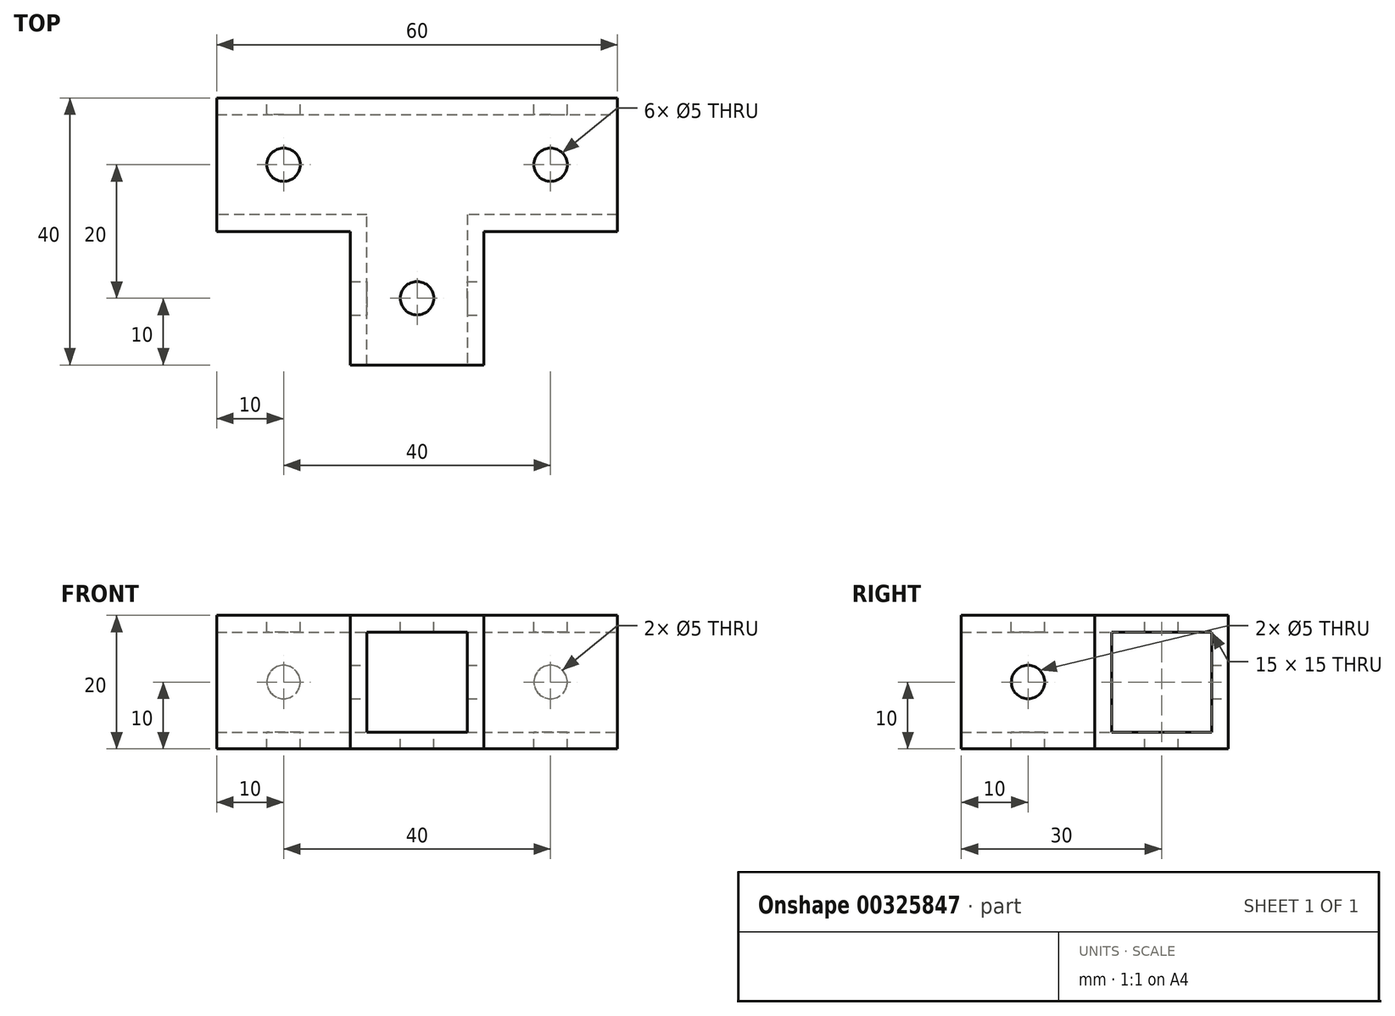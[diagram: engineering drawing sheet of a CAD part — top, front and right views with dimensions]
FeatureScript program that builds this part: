
annotation { "Feature Type Name" : "Feature", "Feature Type Description" : "" }
export const myFeature = defineFeature(function(context is Context, id is Id, definition is map)
    precondition{}
    {
        {
            var Q0;
            Q0=qCreatedBy(makeId("Top.planeOp"),FACE);
            var sketch = newSketch(context, id + "F0", { "sketchPlane" : qUnion([Q0])});
            skLineSegment(sketch, "E0", {"start": v(-30, 0) * mm, "end": v(30, 0) * mm});
            skLineSegment(sketch, "E1", {"start": v(30, 0) * mm, "end": v(30, -20) * mm});
            skLineSegment(sketch, "E2", {"start": v(30, -20) * mm, "end": v(10, -20) * mm});
            skLineSegment(sketch, "E3", {"start": v(10, -20) * mm, "end": v(10, -40) * mm});
            skLineSegment(sketch, "E4", {"start": v(10, -40) * mm, "end": v(-10, -40) * mm});
            skLineSegment(sketch, "E5", {"start": v(-10, -40) * mm, "end": v(-10, -20) * mm});
            skLineSegment(sketch, "E6", {"start": v(-10, -20) * mm, "end": v(-30, -20) * mm});
            skLineSegment(sketch, "E7", {"start": v(-30, -20) * mm, "end": v(-30, 0) * mm});
            skSolve(sketch);
        }
        {
            var Q0;
            Q0 = qSketchRegion(id + "F0", true);
            extrude(context, id + "F1", {"entities" : qUnion([Q0]), "oppositeDirection" : true, "depth" : 20 * mm});
        }
        {
            var Q0;
            Q0=makeQuery(id+"F1.opExtrude","SWEPT_FACE",FACE,{"disambiguationData":[OSD([sQuery(id+"F0.wireOp",EDGE,"E1")])]});
            var Q1;
            Q1=makeQuery(id+"F1.opExtrude","SWEPT_FACE",FACE,{"disambiguationData":[OSD([sQuery(id+"F0.wireOp",EDGE,"E4")])]});
            var Q2;
            Q2=makeQuery(id+"F1.opExtrude","SWEPT_FACE",FACE,{"disambiguationData":[OSD([sQuery(id+"F0.wireOp",EDGE,"E7")])]});
            shell(context, id + "F2", {"entities" : qUnion([Q0, Q1, Q2]), "thickness" : 2.5 * mm});
        }
        {
            var Q0;
            Q0=makeQuery(id+"F1.opExtrude","CAP_FACE",FACE,{"disambiguationData":[OSD([sQuery(id+"F0.wireOp",EDGE,"E0"),sQuery(id+"F0.wireOp",EDGE,"E1"),sQuery(id+"F0.wireOp",EDGE,"E2"),sQuery(id+"F0.wireOp",EDGE,"E3"),sQuery(id+"F0.wireOp",EDGE,"E4"),sQuery(id+"F0.wireOp",EDGE,"E5"),sQuery(id+"F0.wireOp",EDGE,"E6"),sQuery(id+"F0.wireOp",EDGE,"E7")])],"isStart":true});
            var sketch = newSketch(context, id + "F3", { "sketchPlane" : qUnion([Q0])});
            skLineSegment(sketch, "E8", {"start": v(-10, -20) * mm, "end": v(-10, 0) * mm, "construction": true});
            skLineSegment(sketch, "E9", {"start": v(-10, -20) * mm, "end": v(10, -20) * mm, "construction": true});
            skLineSegment(sketch, "E10", {"start": v(10, -20) * mm, "end": v(10, 0) * mm, "construction": true});
            skLineSegment(sketch, "E11", {"start": v(10, 0) * mm, "end": v(30, 0) * mm, "construction": true});
            skLineSegment(sketch, "E12", {"start": v(30, 0) * mm, "end": v(30, -20) * mm, "construction": true});
            skLineSegment(sketch, "E13", {"start": v(30, -20) * mm, "end": v(10, -20) * mm, "construction": true});
            skLineSegment(sketch, "E14", {"start": v(10, -40) * mm, "end": v(10, -20) * mm, "construction": true});
            skLineSegment(sketch, "E15", {"start": v(10, -40) * mm, "end": v(-10, -40) * mm, "construction": true});
            skLineSegment(sketch, "E16", {"start": v(-10, -40) * mm, "end": v(-10, -20) * mm, "construction": true});
            skLineSegment(sketch, "E17", {"start": v(-30, -20) * mm, "end": v(-10, -20) * mm, "construction": true});
            skLineSegment(sketch, "E18", {"start": v(-30, -20) * mm, "end": v(-30, 0) * mm, "construction": true});
            skLineSegment(sketch, "E19", {"start": v(-30, 0) * mm, "end": v(-10, 0) * mm, "construction": true});
            skLineSegment(sketch, "E20", {"start": v(-30, -20) * mm, "end": v(-10, 0) * mm, "construction": true});
            skLineSegment(sketch, "E21", {"start": v(-30, 0) * mm, "end": v(-10, -20) * mm, "construction": true});
            skLineSegment(sketch, "E22", {"start": v(-10, -20) * mm, "end": v(10, -40) * mm, "construction": true});
            skLineSegment(sketch, "E23", {"start": v(10, -20) * mm, "end": v(-10, -40) * mm, "construction": true});
            skLineSegment(sketch, "E24", {"start": v(10, -20) * mm, "end": v(30, 0) * mm, "construction": true});
            skLineSegment(sketch, "E25", {"start": v(10, 0) * mm, "end": v(30, -20) * mm, "construction": true});
            skCircle(sketch, "E26", {"center": v(-20, -10) * mm, "radius": 2.5 * mm});
            skCircle(sketch, "E27", {"center": v(20, -10) * mm, "radius": 2.5 * mm});
            skCircle(sketch, "E28", {"center": v(0, -30) * mm, "radius": 2.5 * mm});
            skSolve(sketch);
        }
        {
            var Q0;
            Q0 = qSketchRegion(id + "F3", true);
            extrude(context, id + "F4", {"entities" : qUnion([Q0]), "operationType" : NewBodyOperationType.REMOVE, "endBound" : BoundingType.THROUGH_ALL, "oppositeDirection" : true, "depth" : 25 * mm});
        }
        {
            var Q0;
            Q0=makeQuery(id+"F1.opExtrude","SWEPT_FACE",FACE,{"disambiguationData":[OSD([sQuery(id+"F0.wireOp",EDGE,"E0")])]});
            var sketch = newSketch(context, id + "F5", { "sketchPlane" : qUnion([Q0])});
            skLineSegment(sketch, "E29", {"start": v(-30, 0) * mm, "end": v(-10, 0) * mm, "construction": true});
            skLineSegment(sketch, "E30", {"start": v(-10, 0) * mm, "end": v(-10, -20) * mm, "construction": true});
            skLineSegment(sketch, "E31", {"start": v(-10, -20) * mm, "end": v(-30, -20) * mm, "construction": true});
            skLineSegment(sketch, "E32", {"start": v(-30, -20) * mm, "end": v(-30, 0) * mm, "construction": true});
            skLineSegment(sketch, "E33", {"start": v(30, 0) * mm, "end": v(30, -20) * mm, "construction": true});
            skLineSegment(sketch, "E34", {"start": v(30, -20) * mm, "end": v(10, -20) * mm, "construction": true});
            skLineSegment(sketch, "E35", {"start": v(10, -20) * mm, "end": v(10, 0) * mm, "construction": true});
            skLineSegment(sketch, "E36", {"start": v(10, 0) * mm, "end": v(30, 0) * mm, "construction": true});
            skLineSegment(sketch, "E37", {"start": v(10, 0) * mm, "end": v(30, -20) * mm, "construction": true});
            skLineSegment(sketch, "E38", {"start": v(30, 0) * mm, "end": v(10, -20) * mm, "construction": true});
            skLineSegment(sketch, "E39", {"start": v(-30, 0) * mm, "end": v(-10, -20) * mm, "construction": true});
            skLineSegment(sketch, "E40", {"start": v(-10, 0) * mm, "end": v(-30, -20) * mm, "construction": true});
            skCircle(sketch, "E41", {"center": v(-20, -10) * mm, "radius": 2.5 * mm});
            skCircle(sketch, "E42", {"center": v(20, -10) * mm, "radius": 2.5 * mm});
            skSolve(sketch);
        }
        {
            var Q0;
            Q0 = qSketchRegion(id + "F5", true);
            extrude(context, id + "F6", {"entities" : qUnion([Q0]), "operationType" : NewBodyOperationType.REMOVE, "endBound" : BoundingType.UP_TO_NEXT, "oppositeDirection" : true, "depth" : 25 * mm});
        }
        {
            var Q0;
            Q0=makeQuery(id+"F1.opExtrude","SWEPT_FACE",FACE,{"disambiguationData":[OSD([sQuery(id+"F0.wireOp",EDGE,"E3")])]});
            var sketch = newSketch(context, id + "F7", { "sketchPlane" : qUnion([Q0])});
            skLineSegment(sketch, "E43", {"start": v(-40, 0) * mm, "end": v(-20, 0) * mm, "construction": true});
            skLineSegment(sketch, "E44", {"start": v(-20, 0) * mm, "end": v(-20, -20) * mm, "construction": true});
            skLineSegment(sketch, "E45", {"start": v(-20, -20) * mm, "end": v(-40, -20) * mm, "construction": true});
            skLineSegment(sketch, "E46", {"start": v(-40, -20) * mm, "end": v(-40, 0) * mm, "construction": true});
            skLineSegment(sketch, "E47", {"start": v(-20, -20) * mm, "end": v(-40, 0) * mm, "construction": true});
            skLineSegment(sketch, "E48", {"start": v(-20, 0) * mm, "end": v(-40, -20) * mm, "construction": true});
            skCircle(sketch, "E49", {"center": v(-30, -10) * mm, "radius": 2.5 * mm});
            skSolve(sketch);
        }
        {
            var Q0;
            Q0 = qSketchRegion(id + "F7", true);
            extrude(context, id + "F8", {"entities" : qUnion([Q0]), "operationType" : NewBodyOperationType.REMOVE, "endBound" : BoundingType.THROUGH_ALL, "oppositeDirection" : true, "depth" : 25 * mm});
        }
    });
